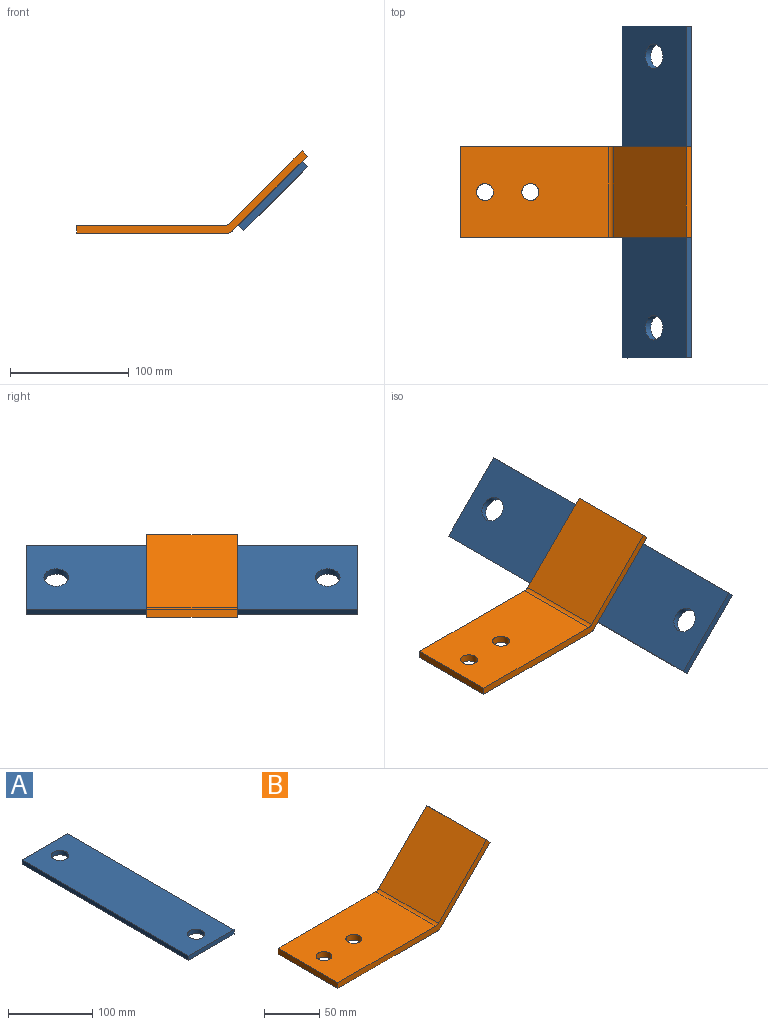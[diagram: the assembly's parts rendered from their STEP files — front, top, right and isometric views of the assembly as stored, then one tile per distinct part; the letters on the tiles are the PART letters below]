
ASSEMBLY  parts=2 mates=1
PART A: 8 faces, bbox 76.2x279.4x6.4 mm
  f0: plane 279.4x6.35mm, normal (1,0,0), area 1774.2mm2, adj f1,f4,f6,f7
  f1: plane 76.2x6.35mm, normal (0,1,0), area 483.9mm2, adj f0,f2,f6,f7
  f2: plane 279.4x6.35mm, normal (-1,0,0), area 1774.2mm2, adj f1,f4,f6,f7
  f3: cylinder r=10.31mm len=20.63mm, axis (0,0,-1), area 411.4mm2, adj f6,f7
  f4: plane 76.2x6.35mm, normal (0,-1,0), area 483.9mm2, adj f0,f2,f6,f7
  f5: cylinder r=10.31mm len=20.63mm, axis (0,0,-1), area 411.4mm2, adj f6,f7
  f6: plane 279.4x76.2mm, normal (0,0,1), area 20622.1mm2, adj f0,f1,f2,f3,f4,f5
  f7: plane 279.4x76.2mm, normal (0,0,-1), area 20622.1mm2, adj f0,f1,f2,f3,f4,f5
PART B: 12 faces, bbox 194.4x76.2x69.2 mm
  f0: plane 76.2x62.86mm, normal (0.71,0,-0.71), area 6774.2mm2, adj f1,f6,f7,f9
  f1: plane 76.2x4.49mm, normal (0.71,0,0.71), area 483.9mm2, adj f0,f2,f6,f7
  f2: plane 76.2x61.37mm, normal (-0.71,0,0.71), area 6613.8mm2, adj f1,f6,f7,f8
  f3: plane 124.9x76.2mm, normal (0,0,1), area 9196.4mm2, adj f4,f6,f7,f8,f10,f11
  f4: plane 76.2x6.35mm, normal (-1,0,0), area 483.9mm2, adj f3,f5,f6,f7
  f5: plane 127x76.2mm, normal (0,0,-1), area 9356.7mm2, adj f4,f6,f7,f9,f10,f11
  f6: plane 194.35x69.21mm, normal (0,-1,0), area 1387.4mm2, adj f0,f1,f2,f3,f4,f5,f8,f9
  f7: plane 194.35x69.21mm, normal (0,1,0), area 1387.4mm2, adj f0,f1,f2,f3,f4,f5,f8,f9
  f8: cylinder r=5.08mm len=76.2mm, axis (0,1,0), area 304mm2, adj f2,f3,f6,f7
  f9: cylinder r=6.35mm len=76.2mm, axis (0,1,0), area 380mm2, adj f0,f5,f6,f7
  f10: cylinder r=7.14mm len=14.29mm, axis (0,0,1), area 285mm2, adj f3,f5
  f11: cylinder r=7.14mm len=14.29mm, axis (0,0,1), area 285mm2, adj f3,f5
PLACE A rot(axis=(0,-1,0),45deg) t=(17.64,-0.29,39.31)mm
PLACE B t=(-22.77,37.81,10.51)mm
MATE fastened A.f6 <-> B.f0  axis (-0.71,0,0.71) through (13.15,-0.29,43.8)mm
